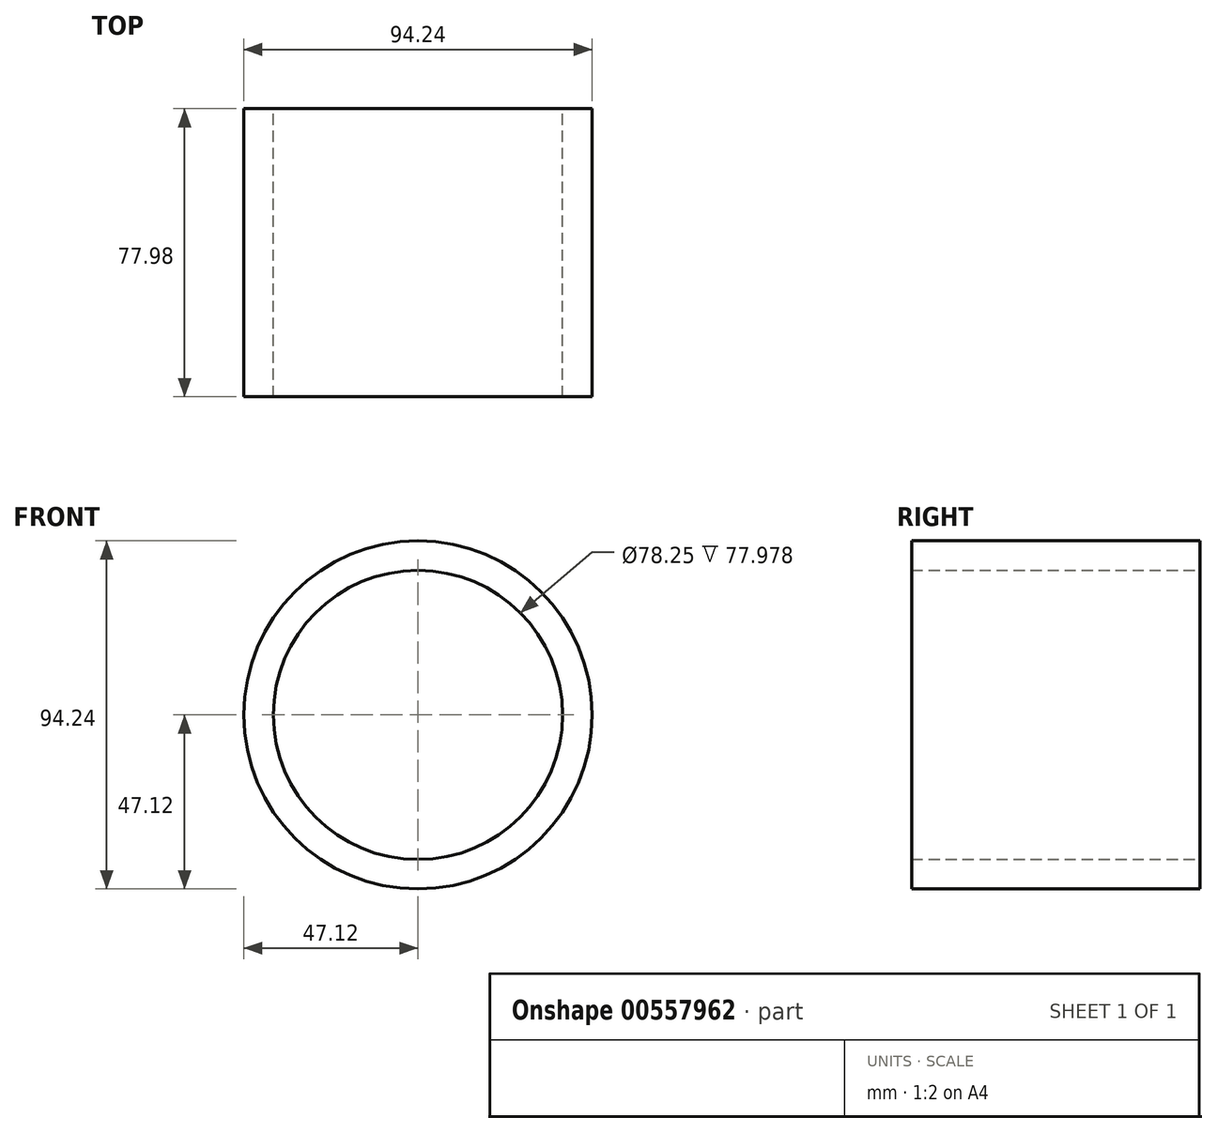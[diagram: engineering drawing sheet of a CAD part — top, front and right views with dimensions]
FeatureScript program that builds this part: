
annotation { "Feature Type Name" : "Feature", "Feature Type Description" : "" }
export const myFeature = defineFeature(function(context is Context, id is Id, definition is map)
    precondition{}
    {
        {
            var Q0;
            Q0=qCreatedBy(makeId("Front.planeOp"),FACE);
            var sketch = newSketch(context, id + "F0", { "sketchPlane" : qUnion([Q0])});
            skCircle(sketch, "E0", {"center": v(0, 0) * mm, "radius": 47.12 * mm});
            skCircle(sketch, "E1", {"center": v(0, 0) * mm, "radius": 39.12 * mm});
            skSolve(sketch);
        }
        {
            var Q0;
            Q0 = qSketchRegion(id + "F0", true);
            extrude(context, id + "F1", {"entities" : qUnion([Q0]), "depth" : 77.98 * mm, "offsetDistance" : 25.4 * mm});
        }
    });
